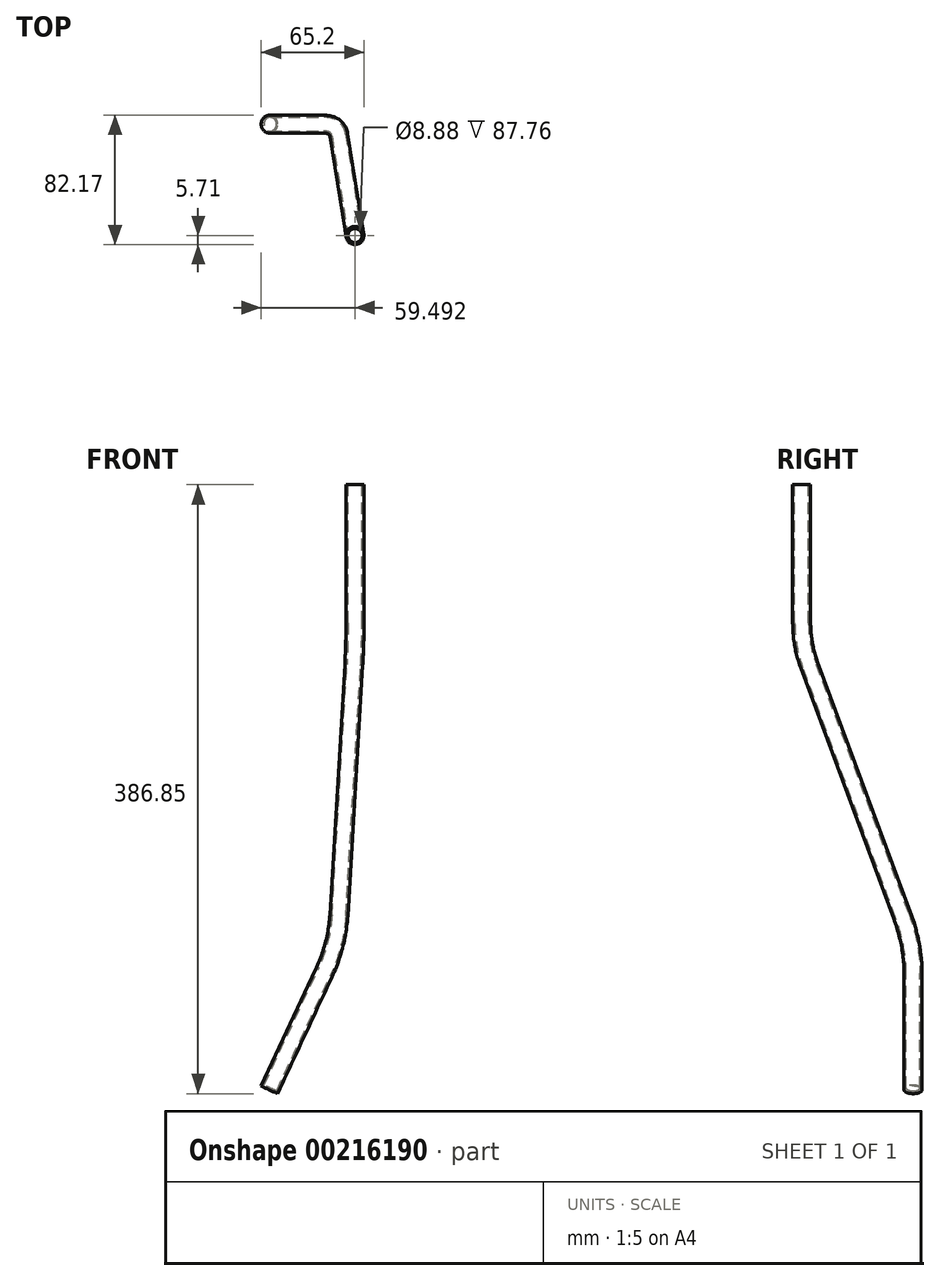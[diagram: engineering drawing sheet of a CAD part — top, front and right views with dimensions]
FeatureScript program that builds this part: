
annotation { "Feature Type Name" : "Feature", "Feature Type Description" : "" }
export const myFeature = defineFeature(function(context is Context, id is Id, definition is map)
    precondition{}
    {
        {
            var Q0;
            Q0=qCreatedBy(makeId("Top.planeOp"),FACE);
            var sketch = newSketch(context, id + "F0", { "sketchPlane" : qUnion([Q0])});
            skLineSegment(sketch, "E0", {"start": v(0, 0) * mm, "end": v(-43.98, 0) * mm});
            skLineSegment(sketch, "E1", {"start": v(-43.98, 0) * mm, "end": v(-43.98, 187.32) * mm});
            skLineSegment(sketch, "E2", {"start": v(-43.98, 187.32) * mm, "end": v(-18.58, 187.32) * mm});
            skSolve(sketch);
        }
        {
            var Q0;
            Q0=sQuery(id+"F0.wireOp",EDGE,"E2");
            cPlane(context, id + "F1", {"entities" : qUnion([Q0]), "cplaneType" : CPlaneType.LINE_ANGLE, "offset" : 25.4 * mm, "angle" : 0 * degree, "width" : 152.4 * mm, "height" : 152.4 * mm});
        }
        {
            var Q0;
            Q0=qCreatedBy(id+"F1.planeOp",FACE);
            var sketch = newSketch(context, id + "F2", { "sketchPlane" : qUnion([Q0])});
            skLineSegment(sketch, "E3", {"start": v(43.98, 0) * mm, "end": v(43.98, -337.88) * mm});
            skLineSegment(sketch, "E4", {"start": v(43.98, -337.88) * mm, "end": v(18.58, -337.88) * mm});
            skSolve(sketch);
        }
        {
            var Q0;
            Q0=sQuery(id+"F2.wireOp",EDGE,"E4");
            cPlane(context, id + "F3", {"entities" : qUnion([Q0]), "cplaneType" : CPlaneType.LINE_ANGLE, "offset" : 25.4 * mm, "angle" : 90 * degree, "width" : 152.4 * mm, "height" : 152.4 * mm});
        }
        {
            var Q0;
            Q0=qCreatedBy(id+"F3.planeOp",FACE);
            var sketch = newSketch(context, id + "F4", { "sketchPlane" : qUnion([Q0])});
            skCircle(sketch, "E5", {"center": v(-43.98, 187.32) * mm, "radius": 5.7 * mm});
            skSolve(sketch);
        }
        {
            var Q0;
            Q0=qCreatedBy(makeId("Top.planeOp"),FACE);
            var sketch = newSketch(context, id + "F5", { "sketchPlane" : qUnion([Q0])});
            skLineSegment(sketch, "E6", {"start": v(0, 0) * mm, "end": v(-98.3, 0) * mm});
            skLineSegment(sketch, "E7", {"start": v(-98.3, 0) * mm, "end": v(-98.3, 258.07) * mm});
            skLineSegment(sketch, "E8", {"start": v(-98.3, 258.07) * mm, "end": v(-72.9, 258.07) * mm});
            skSolve(sketch);
        }
        {
            var Q0;
            Q0=sQuery(id+"F5.wireOp",EDGE,"E8");
            cPlane(context, id + "F6", {"entities" : qUnion([Q0]), "cplaneType" : CPlaneType.LINE_ANGLE, "offset" : 25.4 * mm, "angle" : 0 * degree, "width" : 152.4 * mm, "height" : 152.4 * mm});
        }
        {
            var Q0;
            Q0=qCreatedBy(id+"F6.planeOp",FACE);
            var sketch = newSketch(context, id + "F7", { "sketchPlane" : qUnion([Q0])});
            skLineSegment(sketch, "E9", {"start": v(98.3, 0) * mm, "end": v(98.3, -722.32) * mm});
            skLineSegment(sketch, "E10", {"start": v(98.3, -722.32) * mm, "end": v(72.9, -722.32) * mm});
            skLineSegment(sketch, "E11", {"start": v(98.3, -722.32) * mm, "end": v(70.49, -705.38) * mm});
            skLineSegment(sketch, "E12", {"start": v(98.3, -722.32) * mm, "end": v(123.7, -722.32) * mm});
            skLineSegment(sketch, "E13", {"start": v(98.3, -722.32) * mm, "end": v(137.65, -703.97) * mm});
            skSolve(sketch);
        }
        {
            var Q0;
            Q0=sQuery(id+"F7.wireOp",EDGE,"E13");
            cPlane(context, id + "F8", {"entities" : qUnion([Q0]), "cplaneType" : CPlaneType.LINE_ANGLE, "offset" : 25.4 * mm, "angle" : 90 * degree, "width" : 152.4 * mm, "height" : 152.4 * mm});
        }
        {
            var Q0;
            Q0=qCreatedBy(id+"F8.planeOp",FACE);
            var sketch = newSketch(context, id + "F9", { "sketchPlane" : qUnion([Q0])});
            skCircle(sketch, "E14", {"center": v(216.18, 258.07) * mm, "radius": 5.7 * mm});
            skSolve(sketch);
        }
        {
            var Q0;
            Q0=sQuery(id+"F2.wireOp",EDGE,"E4");
            cPlane(context, id + "F10", {"entities" : qUnion([Q0]), "cplaneType" : CPlaneType.LINE_ANGLE, "offset" : 25.4 * mm, "angle" : 0 * degree, "width" : 152.4 * mm, "height" : 152.4 * mm});
        }
        {
            var Q0;
            Q0=qCreatedBy(id+"F10.planeOp",FACE);
            var sketch = newSketch(context, id + "F11", { "sketchPlane" : qUnion([Q0])});
            skLineSegment(sketch, "E15", {"start": v(43.98, -337.88) * mm, "end": v(43.98, -439.48) * mm});
            skSolve(sketch);
        }
        {
            var Q0;
            Q0=sQuery(id+"F7.wireOp",EDGE,"E13");
            cPlane(context, id + "F12", {"entities" : qUnion([Q0]), "cplaneType" : CPlaneType.LINE_ANGLE, "offset" : 25.4 * mm, "angle" : 0 * degree, "width" : 152.4 * mm, "height" : 152.4 * mm});
        }
        {
            var Q0;
            Q0=qCreatedBy(id+"F12.planeOp",FACE);
            var sketch = newSketch(context, id + "F13", { "sketchPlane" : qUnion([Q0])});
            skLineSegment(sketch, "E16", {"start": v(-98.3, -722.32) * mm, "end": v(-55.36, -630.24) * mm});
            skSolve(sketch);
        }
        {
            var Q0;
            Q0=sQuery(id+"F11.wireOp",VERTEX,"E15.start");
            var Q1;
            Q1=sQuery(id+"F11.wireOp",VERTEX,"E15.end");
            var Q2;
            Q2=sQuery(id+"F13.wireOp",VERTEX,"E16.end");
            cPlane(context, id + "F14", {"entities" : qUnion([Q0, Q1, Q2]), "cplaneType" : CPlaneType.THREE_POINT, "offset" : 25.4 * mm, "width" : 152.4 * mm, "height" : 152.4 * mm});
        }
        {
            var Q0;
            Q0=qCreatedBy(id+"F14.planeOp",FACE);
            var sketch = newSketch(context, id + "F15", { "sketchPlane" : qUnion([Q0])});
            skLineSegment(sketch, "E17", {"start": v(-196.8, -452.43) * mm, "end": v(-263.58, -630.24) * mm});
            skLineSegment(sketch, "E18", {"start": v(-191.93, -425.64) * mm, "end": v(-191.93, -337.88) * mm});
            skPoint(sketch, "E19.visualSharp", {"position": v(-191.93, -439.48) * mm});
            skArc(sketch, "E19.filletArc", {"start": v(-196.8, -452.43) * mm, "mid": v(-193.15, -439.26) * mm, "end": v(-191.93, -425.64) * mm});
            skSolve(sketch);
        }
        {
            var Q0;
            Q0=sQuery(id+"F15.wireOp",VERTEX,"E17.start");
            var Q1;
            Q1=sQuery(id+"F15.wireOp",VERTEX,"E17.end");
            var Q2;
            Q2=sQuery(id+"F13.wireOp",VERTEX,"E16.start");
            cPlane(context, id + "F16", {"entities" : qUnion([Q0, Q1, Q2]), "cplaneType" : CPlaneType.THREE_POINT, "offset" : 25.4 * mm, "width" : 152.4 * mm, "height" : 152.4 * mm});
        }
        {
            var Q0;
            Q0=qCreatedBy(id+"F16.planeOp",FACE);
            var sketch = newSketch(context, id + "F17", { "sketchPlane" : qUnion([Q0])});
            skLineSegment(sketch, "E20", {"start": v(-104.36, -765.7) * mm, "end": v(-59.3, -697.58) * mm});
            skLineSegment(sketch, "E21", {"start": v(-46.85, -661.1) * mm, "end": v(-34.45, -491.54) * mm});
            skPoint(sketch, "E22.visualSharp", {"position": v(-48.3, -680.97) * mm});
            skArc(sketch, "E22.filletArc", {"start": v(-59.3, -697.58) * mm, "mid": v(-50.72, -680.14) * mm, "end": v(-46.85, -661.1) * mm});
            skSolve(sketch);
        }
        {
            var Q0;
            Q0=makeQuery(id+"F9.imprint","IMPRINT",FACE,{"disambiguationData":[TD([[makeQuery(id+"F9.imprint","IMPRINT",EDGE,{"derivedFrom":sQuery(id+"F9.wireOp",EDGE,"E14")}),1.0]])]});
            var Q1;
            Q1=sQuery(id+"F17.wireOp",EDGE,"E20");
            var Q2;
            Q2=sQuery(id+"F17.wireOp",EDGE,"E22.filletArc");
            var Q3;
            Q3=sQuery(id+"F17.wireOp",EDGE,"E21");
            var Q4;
            Q4=sQuery(id+"F15.wireOp",EDGE,"E19.filletArc");
            var Q5;
            Q5=sQuery(id+"F15.wireOp",EDGE,"E18");
            sweep(context, id + "F18", {"profiles" : qUnion([Q0]), "path" : qUnion([Q1, Q2, Q3, Q4, Q5])});
        }
        {
            var Q0;
            Q0=makeQuery(id+"F18.opSweep","CAP_FACE",FACE,{"disambiguationData":[OSD([sQuery(id+"F9.wireOp",EDGE,"E14"),sQuery(id+"F15.wireOp",VERTEX,"E18.end")])],"isStart":false});
            shell(context, id + "F19", {"entities" : qUnion([Q0]), "thickness" : 1.27 * mm});
        }
    });
